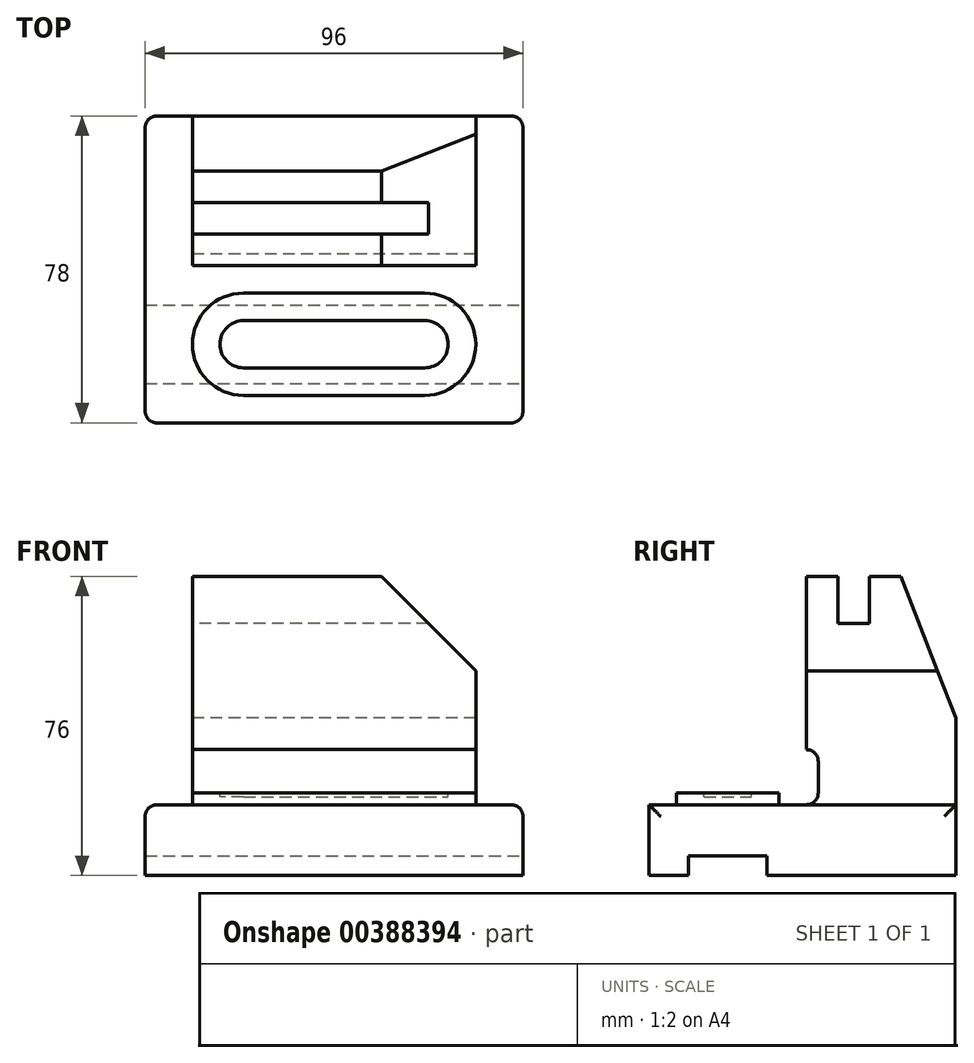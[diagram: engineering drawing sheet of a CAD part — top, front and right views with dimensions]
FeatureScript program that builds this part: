
annotation { "Feature Type Name" : "Feature", "Feature Type Description" : "" }
export const myFeature = defineFeature(function(context is Context, id is Id, definition is map)
    precondition{}
    {
        {
            var Q0;
            Q0=qCreatedBy(makeId("Top.planeOp"),FACE);
            var sketch = newSketch(context, id + "F0", { "sketchPlane" : qUnion([Q0])});
            skLineSegment(sketch, "E0.bottom", {"start": v(0, 0) * mm, "end": v(96, 0) * mm});
            skLineSegment(sketch, "E0.top", {"start": v(0, 78) * mm, "end": v(96, 78) * mm});
            skLineSegment(sketch, "E0.left", {"start": v(0, 0) * mm, "end": v(0, 78) * mm});
            skLineSegment(sketch, "E0.right", {"start": v(96, 0) * mm, "end": v(96, 78) * mm});
            skSolve(sketch);
        }
        {
            var Q0;
            Q0 = qSketchRegion(id + "F0", true);
            extrude(context, id + "F1", {"entities" : qUnion([Q0]), "depth" : 18 * mm});
        }
        {
            var Q0;
            Q0=makeQuery(id+"F1.opExtrude","CAP_FACE",FACE,{"disambiguationData":[OSD([sQuery(id+"F0.wireOp",EDGE,"E0.bottom"),sQuery(id+"F0.wireOp",EDGE,"E0.top"),sQuery(id+"F0.wireOp",EDGE,"E0.left"),sQuery(id+"F0.wireOp",EDGE,"E0.right")])],"isStart":true});
            cPlane(context, id + "F2", {"entities" : qUnion([Q0]), "cplaneType" : CPlaneType.OFFSET, "offset" : 20 * mm, "oppositeDirection" : true, "width" : 150 * mm, "height" : 150 * mm});
        }
        {
            var Q0;
            Q0=makeQuery(id+"F1.opExtrude","CAP_FACE",FACE,{"disambiguationData":[OSD([sQuery(id+"F0.wireOp",EDGE,"E0.bottom"),sQuery(id+"F0.wireOp",EDGE,"E0.top"),sQuery(id+"F0.wireOp",EDGE,"E0.left"),sQuery(id+"F0.wireOp",EDGE,"E0.right")])],"isStart":false});
            var sketch = newSketch(context, id + "F3", { "sketchPlane" : qUnion([Q0])});
            skPoint(sketch, "E1.oppositeSnap0", {"position": v(96, 40) * mm});
            skLineSegment(sketch, "E1.bottom", {"start": v(12, 78) * mm, "end": v(84, 78) * mm});
            skLineSegment(sketch, "E1.top", {"start": v(12, 40) * mm, "end": v(84, 40) * mm});
            skLineSegment(sketch, "E1.left", {"start": v(12, 78) * mm, "end": v(12, 40) * mm});
            skLineSegment(sketch, "E1.right", {"start": v(84, 78) * mm, "end": v(84, 40) * mm});
            skSolve(sketch);
        }
        {
            var Q0;
            Q0=makeQuery(id+"F1.opExtrude","CAP_FACE",FACE,{"disambiguationData":[OSD([sQuery(id+"F0.wireOp",EDGE,"E0.bottom"),sQuery(id+"F0.wireOp",EDGE,"E0.top"),sQuery(id+"F0.wireOp",EDGE,"E0.left"),sQuery(id+"F0.wireOp",EDGE,"E0.right")])],"isStart":true});
            cPlane(context, id + "F4", {"entities" : qUnion([Q0]), "cplaneType" : CPlaneType.OFFSET, "offset" : 76 * mm, "oppositeDirection" : true, "width" : 150 * mm, "height" : 150 * mm});
        }
        {
            var Q0;
            Q0=makeQuery(id+"F3.imprint","IMPRINT",FACE,{"disambiguationData":[TD([[makeQuery(id+"F3.imprint","IMPRINT",EDGE,{"derivedFrom":sQuery(id+"F3.wireOp",EDGE,"E1.bottom")}),-1.0]])]});
            var Q1;
            Q1=qCreatedBy(id+"F4.planeOp",FACE);
            extrude(context, id + "F5", {"entities" : qUnion([Q0]), "operationType" : NewBodyOperationType.ADD, "endBound" : BoundingType.UP_TO_SURFACE, "endBoundEntityFace" : qUnion([Q1]), "depth" : 58 * mm});
        }
        {
            var Q0;
            Q0=makeQuery(id+"F5.opExtrude","SWEPT_FACE",FACE,{"disambiguationData":[OSD([sQuery(id+"F3.wireOp",EDGE,"E1.top")])]});
            var sketch = newSketch(context, id + "F6", { "sketchPlane" : qUnion([Q0])});
            skLineSegment(sketch, "E2", {"start": v(60, 76) * mm, "end": v(84, 52) * mm});
            skLineSegment(sketch, "E3", {"start": v(60, 76) * mm, "end": v(84, 76) * mm});
            skLineSegment(sketch, "E4", {"start": v(84, 52) * mm, "end": v(84, 76) * mm});
            skSolve(sketch);
        }
        {
            var Q0;
            Q0 = qSketchRegion(id + "F6", true);
            var Q1;
            Q1=makeQuery(id+"F5.boolean.opBoolean","MERGE",FACE,{"derivedFrom":[makeQuery(id+"F1.opExtrude","SWEPT_FACE",FACE,{"disambiguationData":[OSD([sQuery(id+"F0.wireOp",EDGE,"E0.top")])]}),makeQuery(id+"F5.opExtrude","SWEPT_FACE",FACE,{"disambiguationData":[OSD([sQuery(id+"F3.wireOp",EDGE,"E1.bottom")])]})]});
            extrude(context, id + "F7", {"entities" : qUnion([Q0]), "operationType" : NewBodyOperationType.REMOVE, "endBound" : BoundingType.UP_TO_SURFACE, "oppositeDirection" : true, "endBoundEntityFace" : qUnion([Q1]), "depth" : 25 * mm});
        }
        {
            var Q0;
            Q0=makeQuery(id+"F5.opExtrude","SWEPT_FACE",FACE,{"disambiguationData":[OSD([sQuery(id+"F3.wireOp",EDGE,"E1.left")])]});
            var sketch = newSketch(context, id + "F8", { "sketchPlane" : qUnion([Q0])});
            skLineSegment(sketch, "E5.bottom", {"start": v(-48, 76) * mm, "end": v(-56, 76) * mm});
            skLineSegment(sketch, "E5.top", {"start": v(-48, 64) * mm, "end": v(-56, 64) * mm});
            skLineSegment(sketch, "E5.left", {"start": v(-48, 76) * mm, "end": v(-48, 64) * mm});
            skLineSegment(sketch, "E5.right", {"start": v(-56, 76) * mm, "end": v(-56, 64) * mm});
            skSolve(sketch);
        }
        {
            var Q0;
            Q0 = qSketchRegion(id + "F8", true);
            extrude(context, id + "F9", {"entities" : qUnion([Q0]), "operationType" : NewBodyOperationType.REMOVE, "endBound" : BoundingType.UP_TO_NEXT, "oppositeDirection" : true, "depth" : 25 * mm});
        }
        {
            var Q0;
            Q0=makeQuery(id+"F5.opExtrude","SWEPT_FACE",FACE,{"disambiguationData":[OSD([sQuery(id+"F3.wireOp",EDGE,"E1.left")])]});
            var sketch = newSketch(context, id + "F10", { "sketchPlane" : qUnion([Q0])});
            skLineSegment(sketch, "E6", {"start": v(-78, 76) * mm, "end": v(-64, 76) * mm});
            skLineSegment(sketch, "E7", {"start": v(-64, 76) * mm, "end": v(-78, 40) * mm});
            skLineSegment(sketch, "E8", {"start": v(-78, 40) * mm, "end": v(-78, 76) * mm});
            skSolve(sketch);
        }
        {
            var Q0;
            Q0 = qSketchRegion(id + "F10", true);
            extrude(context, id + "F11", {"entities" : qUnion([Q0]), "operationType" : NewBodyOperationType.REMOVE, "endBound" : BoundingType.UP_TO_NEXT, "oppositeDirection" : true, "depth" : 25 * mm});
        }
        {
            var Q0;
            Q0=makeQuery(id+"F1.opExtrude","SWEPT_FACE",FACE,{"disambiguationData":[OSD([sQuery(id+"F0.wireOp",EDGE,"E0.right")])]});
            var sketch = newSketch(context, id + "F12", { "sketchPlane" : qUnion([Q0])});
            skLineSegment(sketch, "E9.bottom", {"start": v(10, 0) * mm, "end": v(30, 0) * mm});
            skLineSegment(sketch, "E9.top", {"start": v(10, 5) * mm, "end": v(30, 5) * mm});
            skLineSegment(sketch, "E9.left", {"start": v(10, 0) * mm, "end": v(10, 5) * mm});
            skLineSegment(sketch, "E9.right", {"start": v(30, 0) * mm, "end": v(30, 5) * mm});
            skPoint(sketch, "E10", {"position": v(20, 5) * mm});
            skPoint(sketch, "E11", {"position": v(78, 5) * mm});
            skPoint(sketch, "E12", {"position": v(76.51, 5) * mm});
            skSolve(sketch);
        }
        {
            var Q0;
            Q0 = qSketchRegion(id + "F12", true);
            extrude(context, id + "F13", {"entities" : qUnion([Q0]), "operationType" : NewBodyOperationType.REMOVE, "endBound" : BoundingType.THROUGH_ALL, "oppositeDirection" : true, "depth" : 25 * mm});
        }
        {
            var Q0;
            Q0=makeQuery(id+"F1.opExtrude","CAP_FACE",FACE,{"disambiguationData":[OSD([sQuery(id+"F0.wireOp",EDGE,"E0.bottom"),sQuery(id+"F0.wireOp",EDGE,"E0.top"),sQuery(id+"F0.wireOp",EDGE,"E0.left"),sQuery(id+"F0.wireOp",EDGE,"E0.right")])],"isStart":false});
            var sketch = newSketch(context, id + "F14", { "sketchPlane" : qUnion([Q0])});
            skLineSegment(sketch, "E13.bottom", {"start": v(25, 33) * mm, "end": v(71, 33) * mm});
            skLineSegment(sketch, "E13.top", {"start": v(25, 7) * mm, "end": v(71, 7) * mm});
            skLineSegment(sketch, "E13.left", {"start": v(25, 33) * mm, "end": v(25, 7) * mm});
            skLineSegment(sketch, "E13.right", {"start": v(71, 33) * mm, "end": v(71, 7) * mm});
            skLineSegment(sketch, "E14", {"start": v(25, 20) * mm, "end": v(71, 20) * mm, "construction": true});
            skArc(sketch, "E15", {"start": v(71, 7) * mm, "mid": v(84, 20) * mm, "end": v(71, 33) * mm});
            skArc(sketch, "E16", {"start": v(25, 33) * mm, "mid": v(12, 20) * mm, "end": v(25, 7) * mm});
            skSolve(sketch);
        }
        {
            var Q0;
            Q0 = qSketchRegion(id + "F14", true);
            extrude(context, id + "F15", {"entities" : qUnion([Q0]), "operationType" : NewBodyOperationType.ADD, "depth" : 3 * mm});
        }
        {
            var Q0;
            Q0=makeQuery(id+"F15.opExtrude","CAP_FACE",FACE,{"disambiguationData":[OSD([sQuery(id+"F14.wireOp",EDGE,"E13.bottom"),sQuery(id+"F14.wireOp",EDGE,"E13.top"),sQuery(id+"F14.wireOp",EDGE,"E15"),sQuery(id+"F14.wireOp",EDGE,"E16")])],"isStart":false});
            var sketch = newSketch(context, id + "F16", { "sketchPlane" : qUnion([Q0])});
            skLineSegment(sketch, "E17.bottom", {"start": v(25, 26) * mm, "end": v(71, 26) * mm});
            skLineSegment(sketch, "E17.top", {"start": v(25, 14) * mm, "end": v(71, 14) * mm});
            skLineSegment(sketch, "E17.left", {"start": v(25, 26) * mm, "end": v(25, 14) * mm});
            skLineSegment(sketch, "E17.right", {"start": v(71, 26) * mm, "end": v(71, 14) * mm});
            skArc(sketch, "E18", {"start": v(25, 26) * mm, "mid": v(19, 20) * mm, "end": v(25, 14) * mm});
            skArc(sketch, "E19", {"start": v(71, 14) * mm, "mid": v(77, 20) * mm, "end": v(71, 26) * mm});
            skSolve(sketch);
        }
        {
            var Q0;
            Q0 = qSketchRegion(id + "F16", true);
            var Q1;
            Q1=qCreatedBy(id+"F2.planeOp",FACE);
            extrude(context, id + "F17", {"entities" : qUnion([Q0]), "operationType" : NewBodyOperationType.REMOVE, "endBound" : BoundingType.UP_TO_SURFACE, "oppositeDirection" : true, "endBoundEntityFace" : qUnion([Q1]), "depth" : 25 * mm});
        }
        {
            var Q0;
            Q0=makeQuery(id+"F5.opExtrude","SWEPT_FACE",FACE,{"disambiguationData":[OSD([sQuery(id+"F3.wireOp",EDGE,"E1.right")])]});
            var sketch = newSketch(context, id + "F18", { "sketchPlane" : qUnion([Q0])});
            skLineSegment(sketch, "E20.bottom", {"start": v(40, 18) * mm, "end": v(43, 18) * mm});
            skLineSegment(sketch, "E20.top", {"start": v(40, 32) * mm, "end": v(43, 32) * mm});
            skLineSegment(sketch, "E20.left", {"start": v(40, 18) * mm, "end": v(40, 32) * mm});
            skLineSegment(sketch, "E20.right", {"start": v(43, 18) * mm, "end": v(43, 32) * mm});
            skSolve(sketch);
        }
        {
            var Q0;
            Q0 = qSketchRegion(id + "F18", true);
            extrude(context, id + "F19", {"entities" : qUnion([Q0]), "operationType" : NewBodyOperationType.REMOVE, "endBound" : BoundingType.UP_TO_NEXT, "oppositeDirection" : true, "depth" : 25 * mm});
        }
        {
            var Q0;
            Q0=makeQuery(id+"F19.boolean.opBoolean","COPY",EDGE,{"derivedFrom":makeQuery(id+"F19.opExtrude","SWEPT_EDGE",EDGE,{"disambiguationData":[OSD([sQuery(id+"F18.wireOp",EDGE,"E20.top"),sQuery(id+"F18.wireOp",EDGE,"E20.right")])]})});
            var Q1;
            Q1=makeQuery(id+"F19.boolean.opBoolean","COPY",EDGE,{"derivedFrom":makeQuery(id+"F19.opExtrude","SWEPT_EDGE",EDGE,{"disambiguationData":[OSD([sQuery(id+"F3.wireOp",EDGE,"E1.right"),sQuery(id+"F18.wireOp",EDGE,"E20.bottom"),sQuery(id+"F18.wireOp",EDGE,"E20.right")])]})});
            var Q2;
            Q2=makeQuery(id+"F15.opExtrude","CAP_EDGE",EDGE,{"disambiguationData":[OSD([sQuery(id+"F14.wireOp",EDGE,"E13.bottom")])],"isStart":true});
            var Q3;
            Q3=makeQuery(id+"F15.opExtrude","CAP_EDGE",EDGE,{"disambiguationData":[OSD([sQuery(id+"F14.wireOp",EDGE,"E13.top")])],"isStart":true});
            var Q4;
            Q4=makeQuery(id+"F1.opExtrude","CAP_EDGE",EDGE,{"disambiguationData":[OSD([sQuery(id+"F0.wireOp",EDGE,"E0.right")])],"isStart":false});
            var Q5;
            Q5=makeQuery(id+"F1.opExtrude","CAP_EDGE",EDGE,{"disambiguationData":[OSD([sQuery(id+"F0.wireOp",EDGE,"E0.left")])],"isStart":false});
            var Q6;
            Q6=makeQuery(id+"F5.opExtrude","CAP_EDGE",EDGE,{"disambiguationData":[OSD([sQuery(id+"F3.wireOp",EDGE,"E1.right")])],"isStart":true});
            var Q7;
            Q7=makeQuery(id+"F5.opExtrude","CAP_EDGE",EDGE,{"disambiguationData":[OSD([sQuery(id+"F3.wireOp",EDGE,"E1.left")])],"isStart":true});
            var Q8;
            Q8=makeQuery(id+"F1.opExtrude","SWEPT_EDGE",EDGE,{"disambiguationData":[OSD([sQuery(id+"F0.wireOp",EDGE,"E0.bottom"),sQuery(id+"F0.wireOp",EDGE,"E0.right")])]});
            var Q9;
            Q9=makeQuery(id+"F1.opExtrude","SWEPT_EDGE",EDGE,{"disambiguationData":[OSD([sQuery(id+"F0.wireOp",EDGE,"E0.bottom"),sQuery(id+"F0.wireOp",EDGE,"E0.left")])]});
            var Q10;
            Q10=makeQuery(id+"F1.opExtrude","SWEPT_EDGE",EDGE,{"disambiguationData":[OSD([sQuery(id+"F0.wireOp",EDGE,"E0.top"),sQuery(id+"F0.wireOp",EDGE,"E0.left")])]});
            var Q11;
            Q11=makeQuery(id+"F1.opExtrude","SWEPT_EDGE",EDGE,{"disambiguationData":[OSD([sQuery(id+"F0.wireOp",EDGE,"E0.top"),sQuery(id+"F0.wireOp",EDGE,"E0.right")])]});
            fillet(context, id + "F20", {"entities" : qUnion([Q0, Q1, Q2, Q3, Q4, Q5, Q6, Q7, Q8, Q9, Q10, Q11]), "radius" : 3 * mm, "tangentPropagation" : true, "allowEdgeOverflow" : false});
        }
    });
